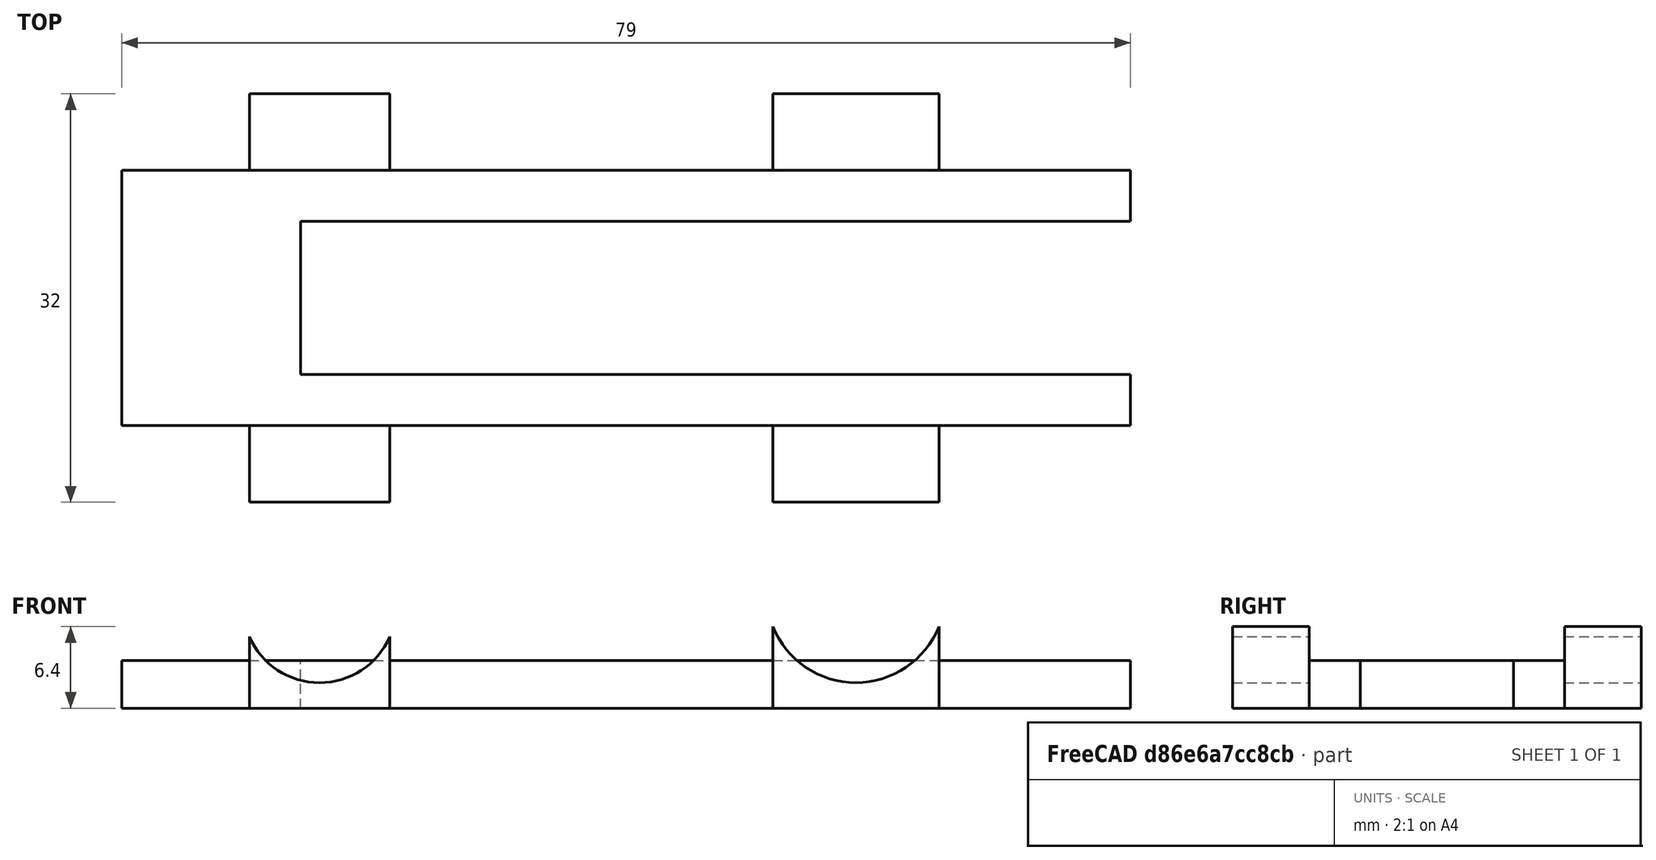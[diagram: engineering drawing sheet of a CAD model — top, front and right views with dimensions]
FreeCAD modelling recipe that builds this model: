
FCSTD DOCUMENT  (FreeCAD 0.19R24276 (Git))
Label: axleJig3
License: All rights reserved
LicenseURL: http://en.wikipedia.org/wiki/All_rights_reserved
objects: Part::Box×5, Part::Cut×4, Part::Cylinder×2, Spreadsheet::Sheet×1, Part::MultiFuse×1
note: 12 computed .brp shape members not serialized (recipe doc carries the construction recipe); baked Part::Feature solids carry a one-line shape summary decoded from their .brp

FEATURE [Part::Box] Box  label="Cube"
  AttacherType = Attacher::AttachEngine3D
  Height = 8
  Length = 11
  Placement = pos=(-5.5,0,0) rot=(0,0,1;0rad)
  Width = 32
  expr: Width = <<data>>.wheel_width * 2 + <<data>>.axle_width
  expr: Length = Spreadsheet.wheel_diameter_F - 1mm
  expr: .Placement.Base.x = -<<data>>.wheel_diameter_F / 2 + 0.5mm
FEATURE [Part::Box] Box008  label="base"
  AttacherType = Attacher::AttachEngine3D
  Height = 3.75
  Length = 79
  Placement = pos=(-15.5,6,0) rot=(0,0,1;0rad)
  Width = 20
  expr: .Placement.Base.y = <<data>>.wheel_width
  expr: Height = <<data>>.ride_height + 2mm
  expr: Width = <<data>>.axle_width
  expr: Length = <<data>>.wheel_diameter_F / 2 + <<data>>.wheel_base + <<data>>.wheel_diameter_R / 2 - 1mm + 25mm
  expr: .Placement.Base.x = -<<data>>.wheel_diameter_F / 2 + 0.5mm - 10mm
FEATURE [Spreadsheet::Sheet] Spreadsheet  label="data"
  cells = A4=wheel_base; B4(wheel_base)==42mm; A5=axle_width; B5(axle_width)==20mm; A6=ride_height; B6(ride_height)==1.75mm; A7=axle_diameter; B7(axle_diameter)==1.75mm; A8=post_wdith; B8(post_wdith)==10mm; A9=post_thickness; B9(post_thickness)==1.5mm; A10=wheel_diameter_F; B10(wheel_diameter_F)==12mm; A11=wheel_diameter_R; B11(wheel_diameter_R)==14mm; A12=wheel_width; B12(wheel_width)==6mm
FEATURE [Part::Cylinder] Cylinder
  Angle = 360
  AttacherType = Attacher::AttachEngine3D
  Height = 32
  Placement = pos=(0,0,8) rot=(-1,0,0;1.5708rad)
  Radius = 6
  expr: Radius = <<data>>.wheel_diameter_F / 2
  expr: Height = <<data>>.wheel_width * 2 + <<data>>.axle_width
  expr: .Placement.Base.z = <<data>>.wheel_diameter_F / 2 + 2mm
FEATURE [Part::Cut] Cut  label="Front Axle"
  Base = -> Box
  Tool = -> Cylinder
FEATURE [Part::Box] Box015  label="Cube015"
  AttacherType = Attacher::AttachEngine3D
  Height = 8
  Length = 13
  Placement = pos=(35.5,0,0) rot=(0,0,1;0rad)
  Width = 32
  expr: .Placement.Base.x = -<<data>>.wheel_diameter_R / 2 + 0.5mm + <<data>>.wheel_base
  expr: Length = Spreadsheet.wheel_diameter_R - 1mm
  expr: Width = <<data>>.wheel_width * 2 + <<data>>.axle_width
FEATURE [Part::Cylinder] Cylinder001
  Angle = 360
  AttacherType = Attacher::AttachEngine3D
  Height = 32
  Placement = pos=(42,0,9) rot=(-1,0,0;1.5708rad)
  Radius = 7
  expr: .Placement.Base.z = <<data>>.wheel_diameter_R / 2 + 2mm
  expr: Height = <<data>>.wheel_width * 2 + <<data>>.axle_width
  expr: Radius = <<data>>.wheel_diameter_R / 2
  expr: .Placement.Base.x = <<data>>.wheel_base
FEATURE [Part::Cut] Cut004  label="RearAxle"
  Base = -> Box015
  Tool = -> Cylinder001
FEATURE [Part::Box] Box016  label="basecutout"
  AttacherType = Attacher::AttachEngine3D
  Height = 10
  Length = 54
  Placement = pos=(-5.5,6,0) rot=(0,0,1;0rad)
  Width = 20
  expr: .Placement.Base.x = -<<data>>.wheel_diameter_F / 2 + 0.5mm
  expr: Length = <<data>>.wheel_diameter_F / 2 + <<data>>.wheel_base + <<data>>.wheel_diameter_R / 2 - 1mm
  expr: Width = <<data>>.axle_width
  expr: .Placement.Base.y = <<data>>.wheel_width
FEATURE [Part::MultiFuse] Fusion  label="Axles"
  Shapes = -> [Cut,Cut004]
FEATURE [Part::Cut] Cut005
  Base = -> Fusion
  Tool = -> Box016
FEATURE [Part::Box] Box017  label="basecutout001"
  AttacherType = Attacher::AttachEngine3D
  Height = 3.75
  Length = 71
  Placement = pos=(-1.5,10,0) rot=(0,0,1;0rad)
  Width = 12
  expr: .Placement.Base.x = -<<data>>.wheel_diameter_F / 2 + 0.5mm + 4mm
  expr: Length = <<data>>.wheel_diameter_F / 2 + <<data>>.wheel_base + <<data>>.wheel_diameter_R / 2 - 1mm - 8mm + 25mm
  expr: Width = <<data>>.axle_width - 8mm
  expr: Height = <<data>>.ride_height + 2mm
  expr: .Placement.Base.y = <<data>>.wheel_width + 4mm
FEATURE [Part::Cut] Cut006
  Base = -> Box008
  Tool = -> Box017
